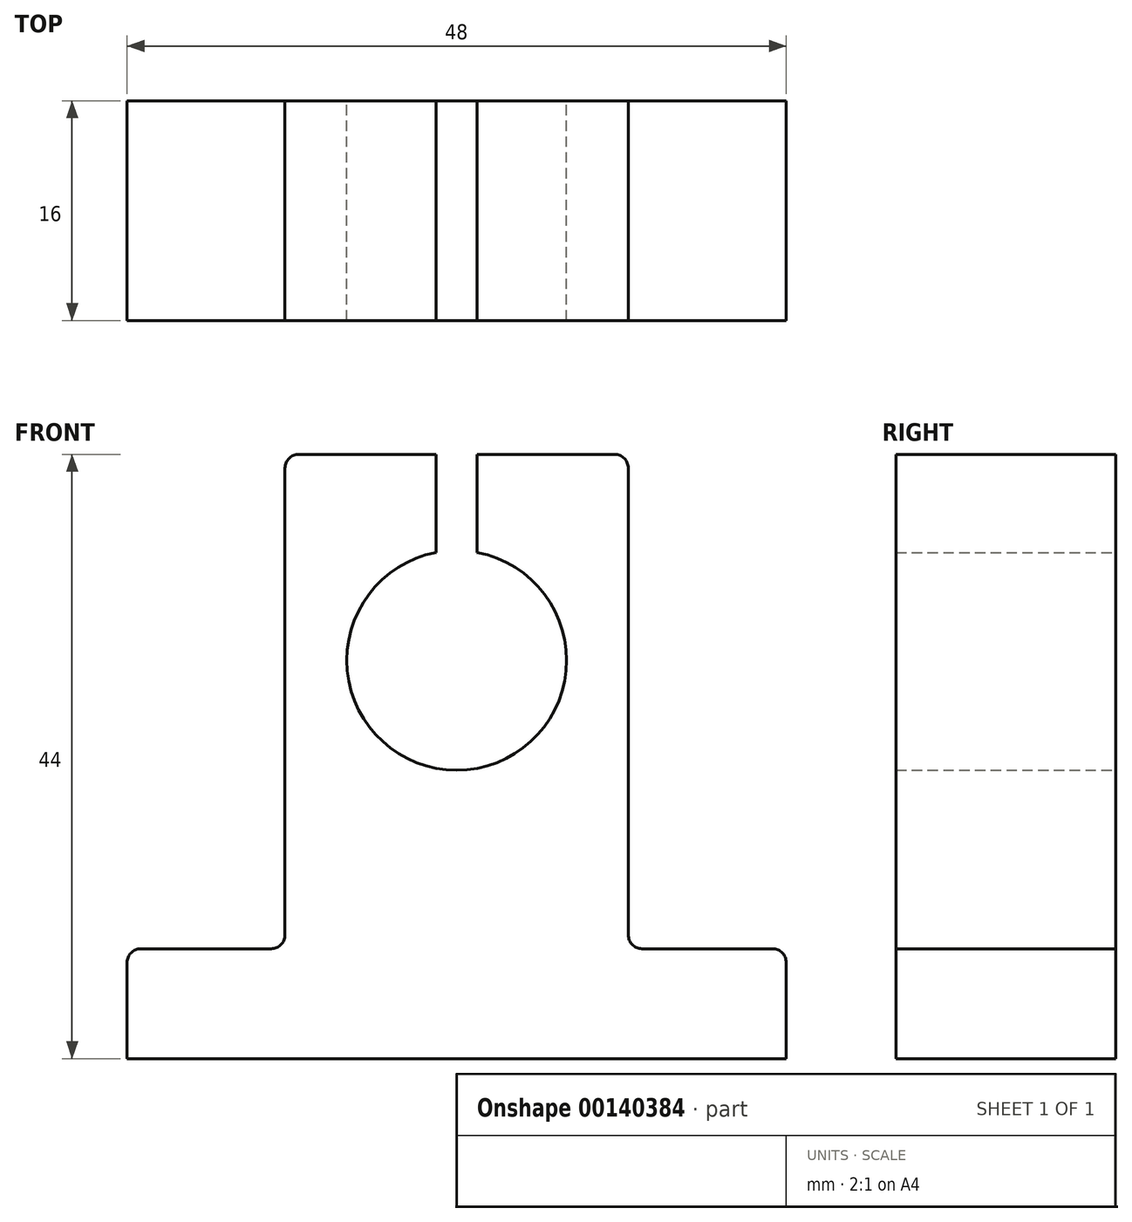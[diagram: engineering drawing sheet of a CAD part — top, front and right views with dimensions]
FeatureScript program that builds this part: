
annotation { "Feature Type Name" : "Feature", "Feature Type Description" : "" }
export const myFeature = defineFeature(function(context is Context, id is Id, definition is map)
    precondition{}
    {
        {
            var Q0;
            Q0=qCreatedBy(makeId("Front.planeOp"),FACE);
            var sketch = newSketch(context, id + "F0", { "sketchPlane" : qUnion([Q0])});
            skLineSegment(sketch, "E0", {"start": v(24, -23.58) * mm, "end": v(-24, -23.58) * mm});
            skLineSegment(sketch, "E1", {"start": v(-24, -23.58) * mm, "end": v(-24, -16.58) * mm});
            skLineSegment(sketch, "E2", {"start": v(-23, -15.58) * mm, "end": v(-13.5, -15.58) * mm});
            skLineSegment(sketch, "E3", {"start": v(-12.5, -14.58) * mm, "end": v(-12.5, 19.42) * mm});
            skLineSegment(sketch, "E4", {"start": v(-11.5, 20.42) * mm, "end": v(-1.5, 20.42) * mm});
            skLineSegment(sketch, "E5", {"start": v(12.5, 19.42) * mm, "end": v(12.5, -14.58) * mm});
            skLineSegment(sketch, "E6", {"start": v(13.5, -15.58) * mm, "end": v(23, -15.58) * mm});
            skLineSegment(sketch, "E7", {"start": v(24, -16.58) * mm, "end": v(24, -23.58) * mm});
            skLineSegment(sketch, "E8", {"start": v(0, 26.96) * mm, "end": v(0, -31.86) * mm, "construction": true});
            skPoint(sketch, "E9.visualSharp", {"position": v(-12.5, 20.42) * mm});
            skArc(sketch, "E9.filletArc", {"start": v(-11.5, 20.42) * mm, "mid": v(-12.2, 20.13) * mm, "end": v(-12.5, 19.42) * mm});
            skPoint(sketch, "E10.visualSharp", {"position": v(12.5, 20.42) * mm});
            skArc(sketch, "E10.filletArc", {"start": v(12.5, 19.42) * mm, "mid": v(12.2, 20.13) * mm, "end": v(11.5, 20.42) * mm});
            skPoint(sketch, "E11.visualSharp", {"position": v(12.5, -15.58) * mm});
            skArc(sketch, "E11.filletArc", {"start": v(12.5, -14.58) * mm, "mid": v(12.8, -15.28) * mm, "end": v(13.5, -15.58) * mm});
            skPoint(sketch, "E12.visualSharp", {"position": v(-12.5, -15.58) * mm});
            skArc(sketch, "E12.filletArc", {"start": v(-13.5, -15.58) * mm, "mid": v(-12.8, -15.28) * mm, "end": v(-12.5, -14.58) * mm});
            skArc(sketch, "E13", {"start": v(-1.5, 13.28) * mm, "mid": v(0, -2.58) * mm, "end": v(1.5, 13.28) * mm});
            skLineSegment(sketch, "E14", {"start": v(-1.5, 20.42) * mm, "end": v(-1.5, 13.28) * mm});
            skLineSegment(sketch, "E15.MirrorCS", {"start": v(1.5, 27.9) * mm, "end": v(1.5, 13.28) * mm});
            skPoint(sketch, "E16.orphan", {"position": v(-1.5, 27.9) * mm});
            skLineSegment(sketch, "E17.trimOffspring", {"start": v(1.5, 20.42) * mm, "end": v(11.5, 20.42) * mm});
            skPoint(sketch, "E18.orphan", {"position": v(1.5, 2.3) * mm});
            skPoint(sketch, "E19.orphan", {"position": v(-1.5, 2.3) * mm});
            skPoint(sketch, "E20.visualSharp", {"position": v(24, -15.58) * mm});
            skArc(sketch, "E20.filletArc", {"start": v(24, -16.58) * mm, "mid": v(23.7, -15.87) * mm, "end": v(23, -15.58) * mm});
            skPoint(sketch, "E21.visualSharp", {"position": v(-24, -15.58) * mm});
            skArc(sketch, "E21.filletArc", {"start": v(-23, -15.58) * mm, "mid": v(-23.7, -15.87) * mm, "end": v(-24, -16.58) * mm});
            skSolve(sketch);
        }
        {
            var Q0;
            Q0 = qSketchRegion(id + "F0", true);
            extrude(context, id + "F1", {"entities" : qUnion([Q0]), "endBound" : BoundingType.SYMMETRIC, "depth" : 16 * mm});
        }
    });
